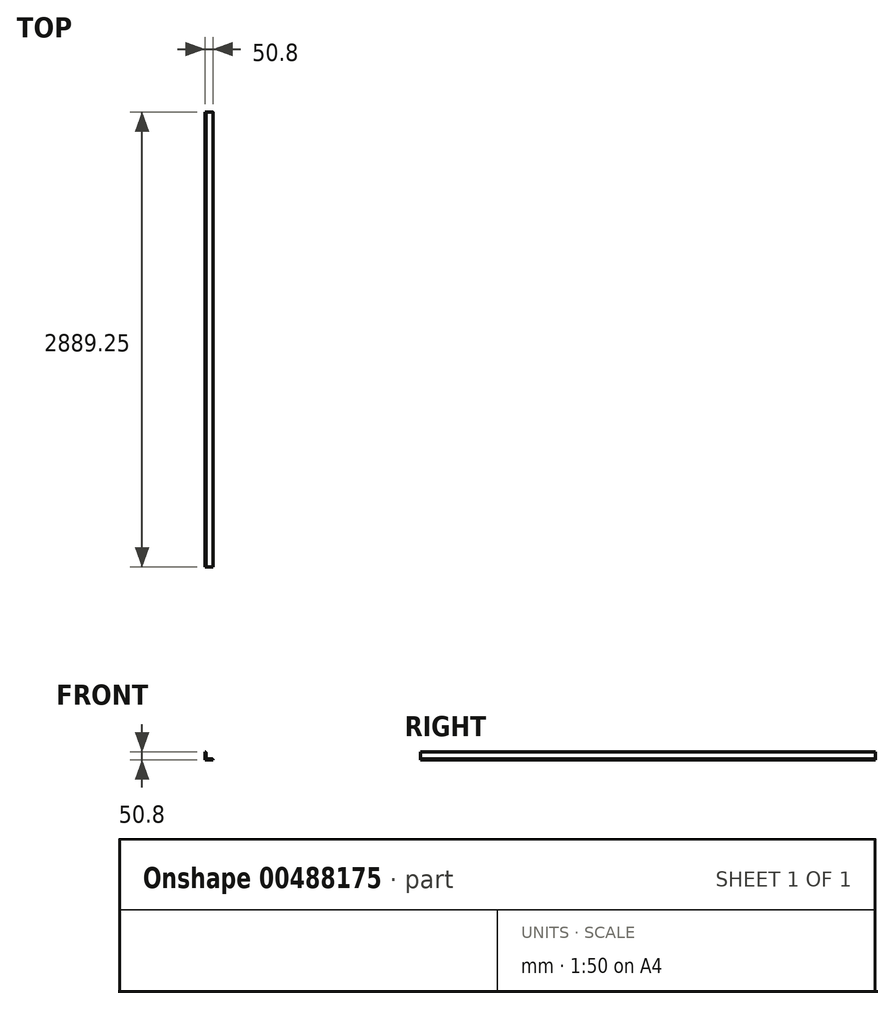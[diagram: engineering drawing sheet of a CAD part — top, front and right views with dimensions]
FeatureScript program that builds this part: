
annotation { "Feature Type Name" : "Feature", "Feature Type Description" : "" }
export const myFeature = defineFeature(function(context is Context, id is Id, definition is map)
    precondition{}
    {
        {
            var Q0;
            Q0=qCreatedBy(makeId("Front.planeOp"),FACE);
            var sketch = newSketch(context, id + "F0", { "sketchPlane" : qUnion([Q0])});
            skLineSegment(sketch, "E0", {"start": v(0, 0) * mm, "end": v(0, 50.8) * mm});
            skLineSegment(sketch, "E1", {"start": v(0, 0) * mm, "end": v(50.8, 0) * mm});
            skLineSegment(sketch, "E2", {"start": v(0, 50.8) * mm, "end": v(0, 50.8) * mm});
            skLineSegment(sketch, "E3", {"start": v(50.8, 0) * mm, "end": v(50.8, 0) * mm});
            skLineSegment(sketch, "E4", {"start": v(44.45, 6.35) * mm, "end": v(6.35, 6.35) * mm});
            skLineSegment(sketch, "E5", {"start": v(6.35, 44.45) * mm, "end": v(6.35, 6.35) * mm});
            skPoint(sketch, "E6.visualSharp", {"position": v(6.35, 50.8) * mm});
            skArc(sketch, "E6.filletArc", {"start": v(6.35, 44.45) * mm, "mid": v(4.5, 48.94) * mm, "end": v(0, 50.8) * mm});
            skPoint(sketch, "E7.visualSharp", {"position": v(50.8, 6.35) * mm});
            skArc(sketch, "E7.filletArc", {"start": v(50.8, 0) * mm, "mid": v(48.94, 4.5) * mm, "end": v(44.45, 6.35) * mm});
            skSolve(sketch);
        }
        {
            var Q0;
            Q0=makeQuery(id+"F0.imprint","IMPRINT",FACE,{"disambiguationData":[TD([[makeQuery(id+"F0.imprint","IMPRINT",EDGE,{"derivedFrom":sQuery(id+"F0.wireOp",EDGE,"E0")}),-1.0]])]});
            extrude(context, id + "F1", {"entities" : qUnion([Q0]), "depth" : 2889.25 * mm, "offsetDistance" : 25.4 * mm});
        }
    });
